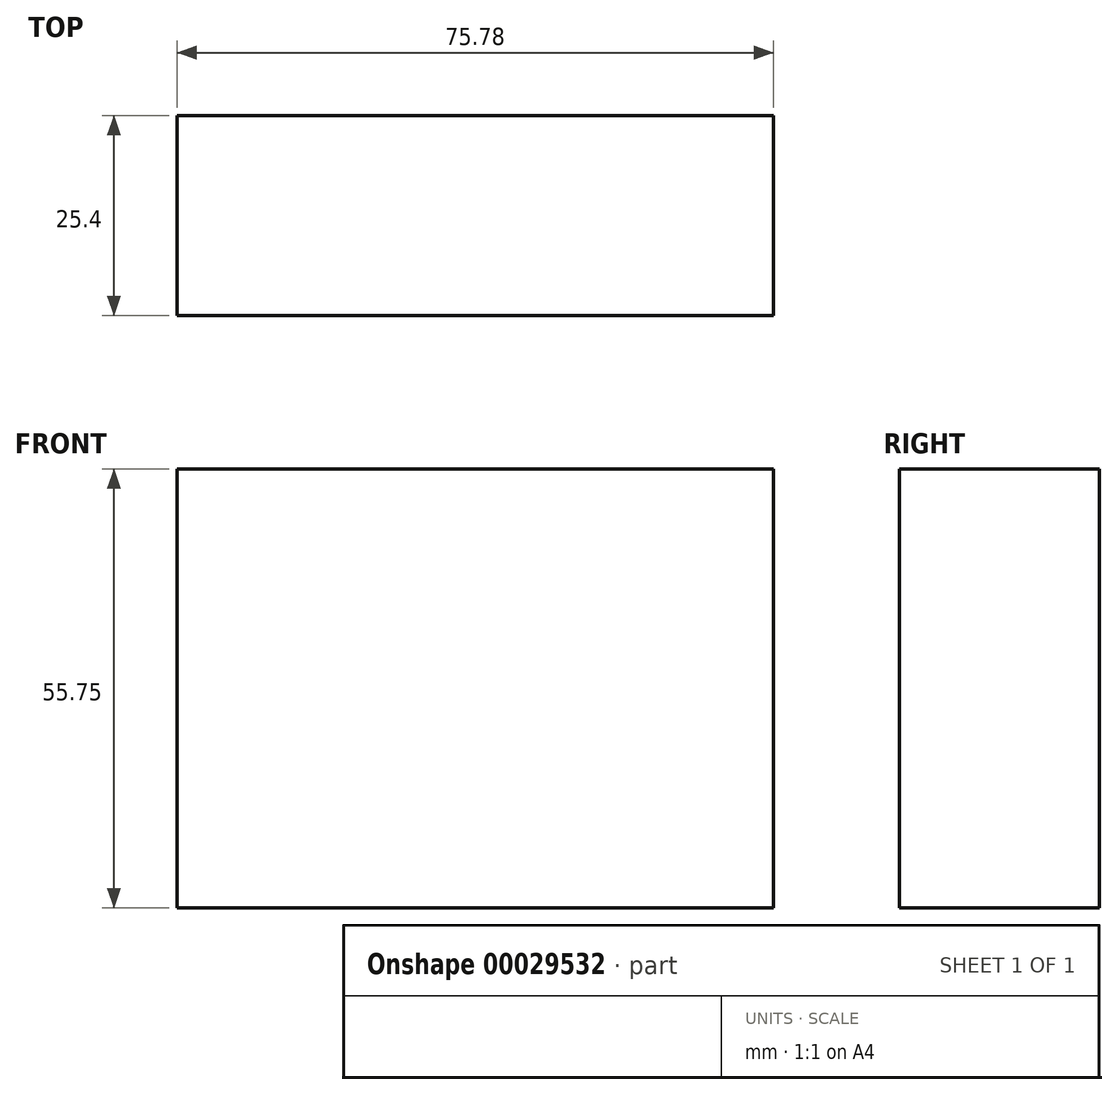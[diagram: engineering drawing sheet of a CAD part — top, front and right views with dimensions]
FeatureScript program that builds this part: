
annotation { "Feature Type Name" : "Feature", "Feature Type Description" : "" }
export const myFeature = defineFeature(function(context is Context, id is Id, definition is map)
    precondition{}
    {
        {
            var Q0;
            Q0=qCreatedBy(makeId("Front.planeOp"),FACE);
            var sketch = newSketch(context, id + "F0", { "sketchPlane" : qUnion([Q0])});
            skLineSegment(sketch, "E0.bottom", {"start": v(0, 0) * mm, "end": v(75.78, 0) * mm});
            skLineSegment(sketch, "E0.top", {"start": v(0, 55.75) * mm, "end": v(75.78, 55.75) * mm});
            skLineSegment(sketch, "E0.left", {"start": v(0, 0) * mm, "end": v(0, 55.75) * mm});
            skLineSegment(sketch, "E0.right", {"start": v(75.78, 0) * mm, "end": v(75.78, 55.75) * mm});
            skSolve(sketch);
        }
        {
            var Q0;
            Q0 = qSketchRegion(id + "F0", true);
            extrude(context, id + "F1", {"entities" : qUnion([Q0]), "depth" : 25.4 * mm});
        }
    });
